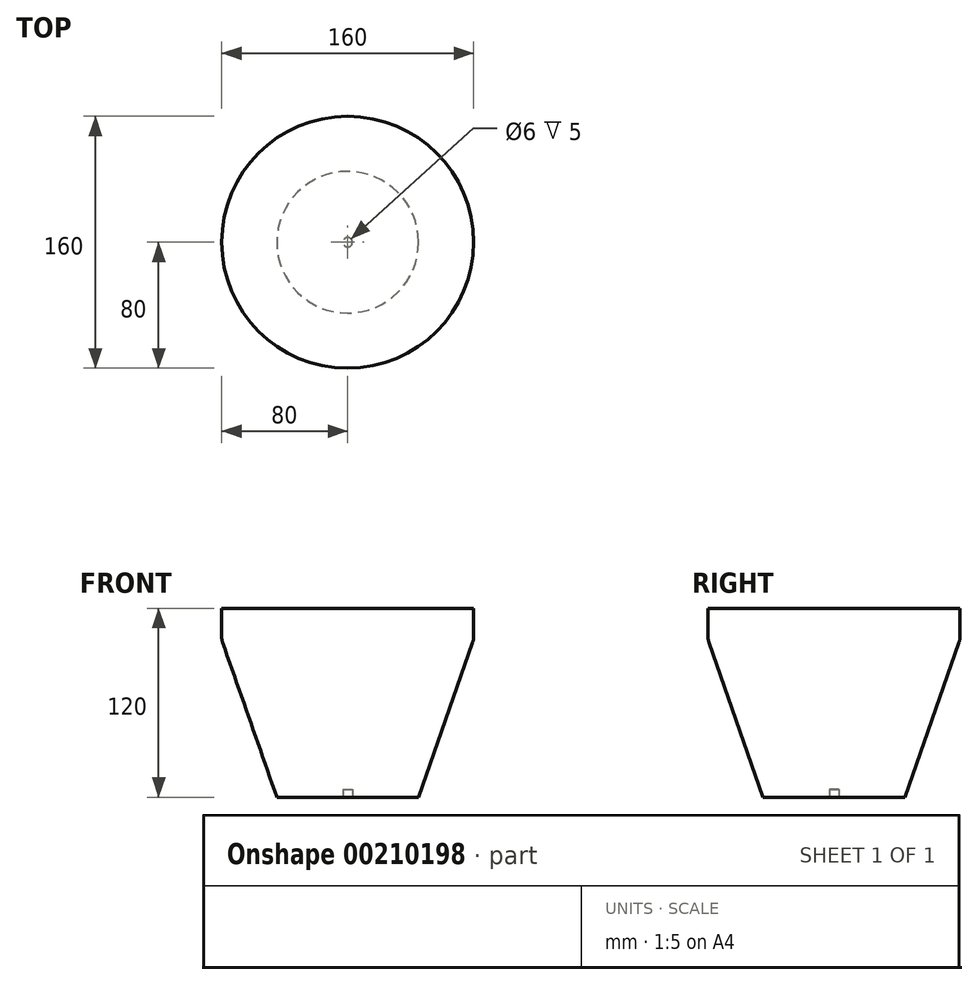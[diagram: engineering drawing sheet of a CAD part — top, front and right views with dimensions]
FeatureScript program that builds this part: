
annotation { "Feature Type Name" : "Feature", "Feature Type Description" : "" }
export const myFeature = defineFeature(function(context is Context, id is Id, definition is map)
    precondition{}
    {
        {
            var Q0;
            Q0=qCreatedBy(makeId("Front.planeOp"),FACE);
            var sketch = newSketch(context, id + "F0", { "sketchPlane" : qUnion([Q0])});
            skLineSegment(sketch, "E0", {"start": v(0, 0) * mm, "end": v(45, 0) * mm});
            skLineSegment(sketch, "E1", {"start": v(45, 0) * mm, "end": v(80, 120) * mm, "construction": true});
            skLineSegment(sketch, "E2", {"start": v(80, 120) * mm, "end": v(0, 120) * mm});
            skLineSegment(sketch, "E3", {"start": v(0, 120) * mm, "end": v(0, 0) * mm});
            skLineSegment(sketch, "E4", {"start": v(0, 120) * mm, "end": v(0, 221.82) * mm, "construction": true});
            skLineSegment(sketch, "E5", {"start": v(80, 120) * mm, "end": v(80, 100) * mm});
            skLineSegment(sketch, "E6", {"start": v(80, 100) * mm, "end": v(45, 0) * mm});
            skSolve(sketch);
        }
        {
            var Q0;
            Q0=makeQuery(id+"F0.imprint","IMPRINT",FACE,{"disambiguationData":[TD([[makeQuery(id+"F0.imprint","IMPRINT",EDGE,{"derivedFrom":sQuery(id+"F0.wireOp",EDGE,"E0")}),1.0]])]});
            var Q1;
            Q1=sQuery(id+"F0.wireOp",EDGE,"E4");
            revolve(context, id + "F1", {"entities" : qUnion([Q0]), "axis" : qUnion([Q1]), "revolveType" : RevolveType.FULL});
        }
        {
            var Q0;
            Q0=makeQuery(id+"F1.opRevolve","SWEPT_FACE",FACE,{"disambiguationData":[OSD([sQuery(id+"F0.wireOp",EDGE,"E0")])]});
            var sketch = newSketch(context, id + "F2", { "sketchPlane" : qUnion([Q0])});
            skCircle(sketch, "E7", {"center": v(0, 0) * mm, "radius": 3 * mm});
            skSolve(sketch);
        }
        {
            var Q0;
            Q0 = qSketchRegion(id + "F2", true);
            extrude(context, id + "F3", {"entities" : qUnion([Q0]), "operationType" : NewBodyOperationType.REMOVE, "oppositeDirection" : true, "depth" : 5 * mm});
        }
        {
            var Q0;
            Q0=makeQuery(id+"F1.opRevolve","SWEPT_EDGE",EDGE,{"disambiguationData":[OSD([sQuery(id+"F0.wireOp",EDGE,"E5"),sQuery(id+"F0.wireOp",EDGE,"E6")])]});
            fillet(context, id + "F4", {"entities" : qUnion([Q0]), "radius" : 10 * mm, "tangentPropagation" : true, "allowEdgeOverflow" : false});
        }
    });
